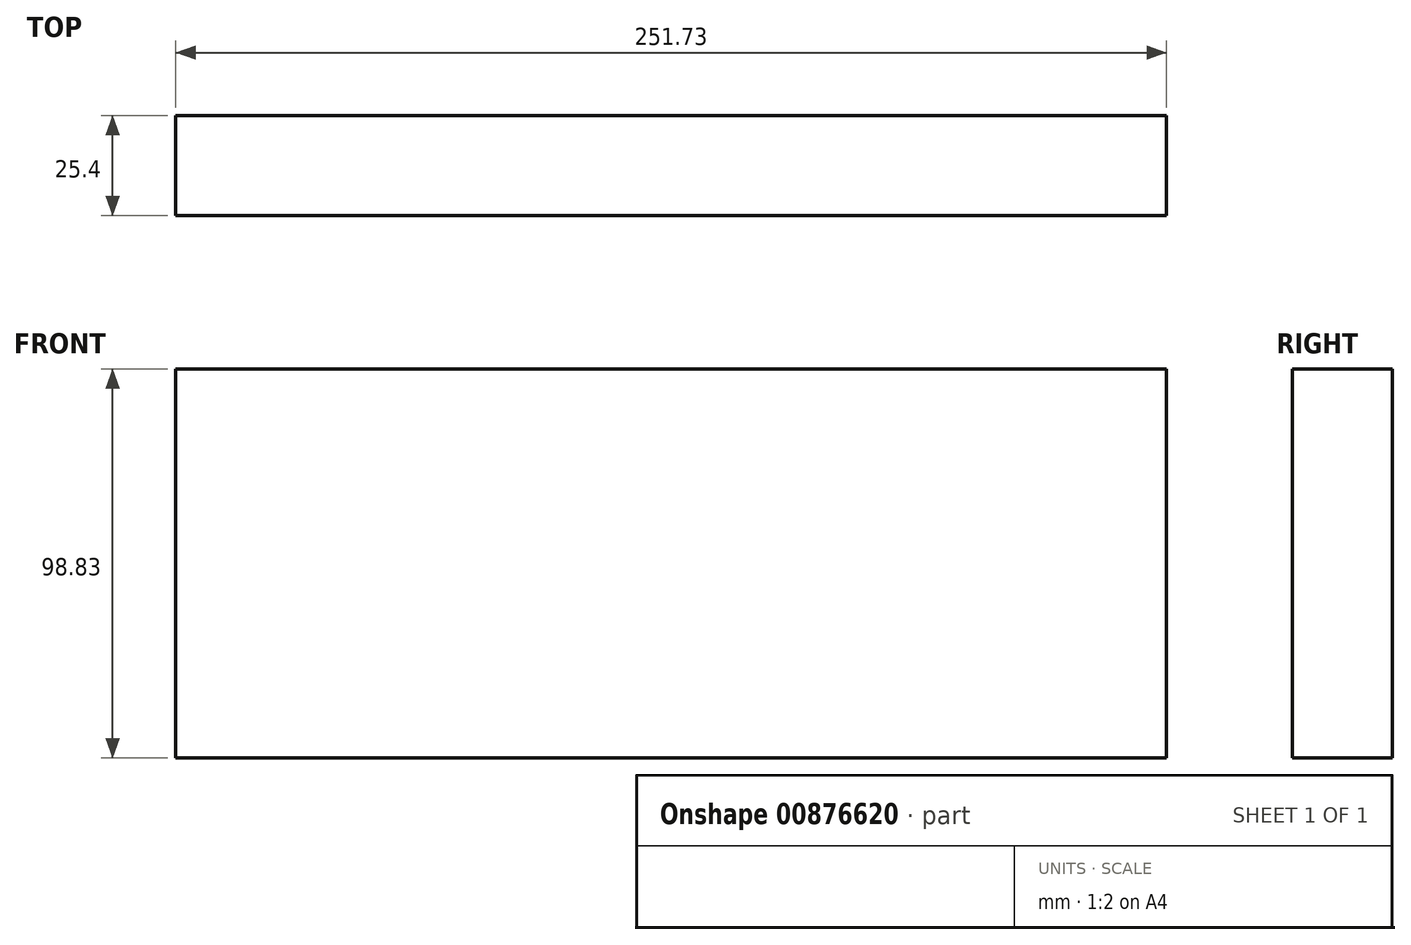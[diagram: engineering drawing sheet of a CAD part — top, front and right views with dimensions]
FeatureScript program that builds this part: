
annotation { "Feature Type Name" : "Feature", "Feature Type Description" : "" }
export const myFeature = defineFeature(function(context is Context, id is Id, definition is map)
    precondition{}
    {
        {
            var Q0;
            Q0=qCreatedBy(makeId("Front.planeOp"),FACE);
            var sketch = newSketch(context, id + "F0", { "sketchPlane" : qUnion([Q0])});
            skLineSegment(sketch, "E0.bottom", {"start": v(-131.5, 48.45) * mm, "end": v(120.23, 48.45) * mm});
            skLineSegment(sketch, "E0.top", {"start": v(-131.5, -50.38) * mm, "end": v(120.23, -50.38) * mm});
            skLineSegment(sketch, "E0.left", {"start": v(-131.5, 48.45) * mm, "end": v(-131.5, -50.38) * mm});
            skLineSegment(sketch, "E0.right", {"start": v(120.23, 48.45) * mm, "end": v(120.23, -50.38) * mm});
            skSolve(sketch);
        }
        {
            var Q0;
            Q0=sQuery(id+"F0.wireOp",EDGE,"E0.bottom");
            var Q1;
            Q1=sQuery(id+"F0.wireOp",EDGE,"E0.left");
            var Q2;
            Q2=sQuery(id+"F0.wireOp",EDGE,"E0.top");
            var Q3;
            Q3=sQuery(id+"F0.wireOp",EDGE,"E0.right");
            extrude(context, id + "F1", {"bodyType" : ToolBodyType.SURFACE, "surfaceEntities" : qUnion([Q0, Q1, Q2, Q3]), "depth" : 25.4 * mm, "offsetDistance" : 25.4 * mm});
        }
    });
